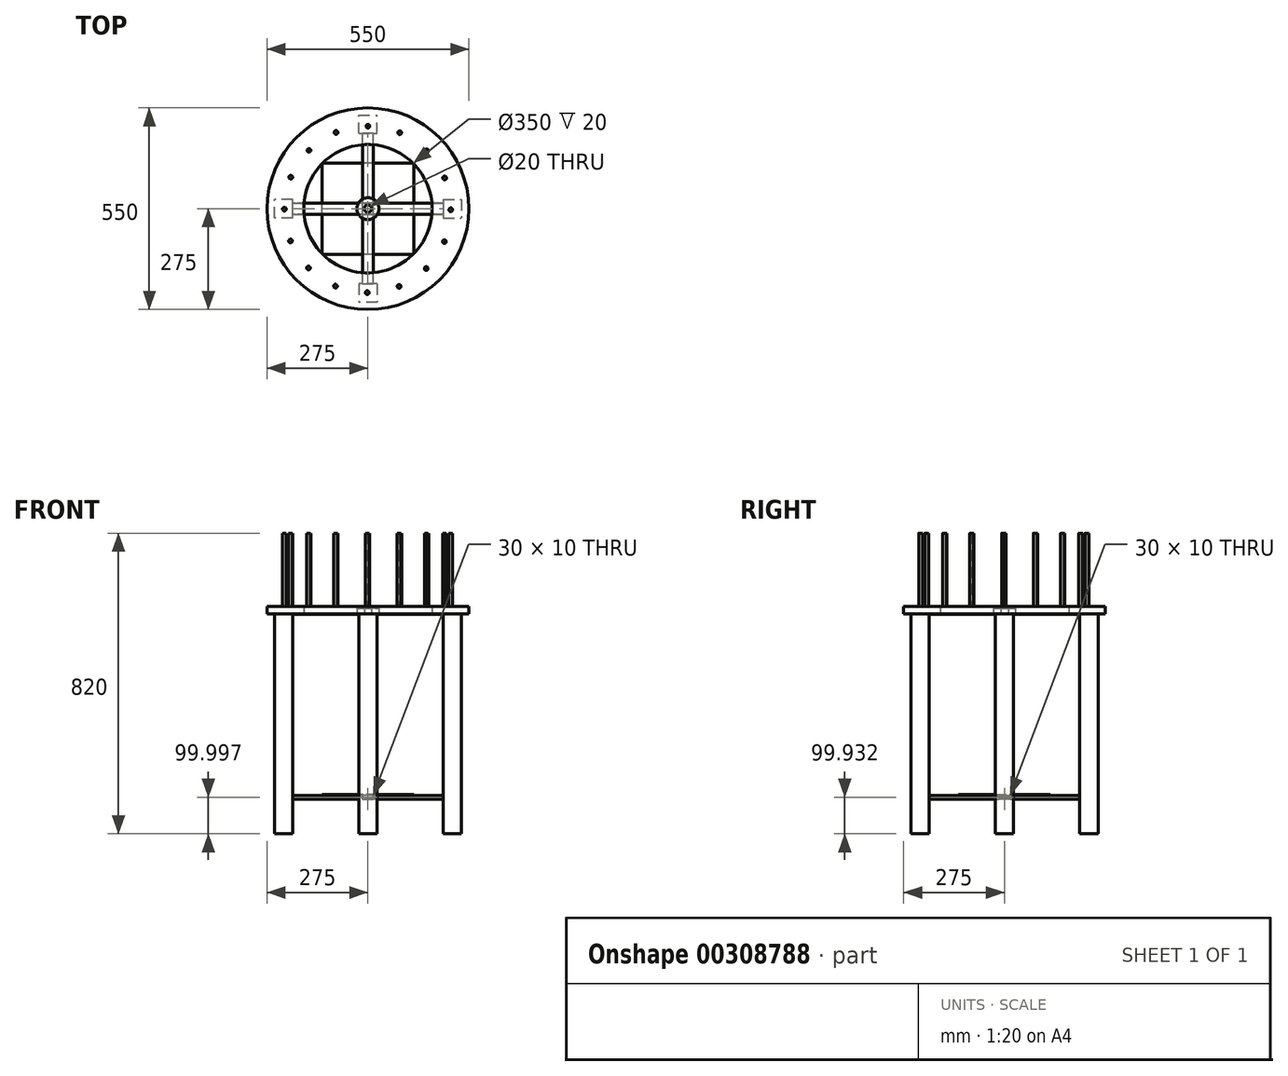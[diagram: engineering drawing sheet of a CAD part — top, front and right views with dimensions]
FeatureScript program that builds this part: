
annotation { "Feature Type Name" : "Feature", "Feature Type Description" : "" }
export const myFeature = defineFeature(function(context is Context, id is Id, definition is map)
    precondition{}
    {
        {
            var Q0;
            Q0=qCreatedBy(makeId("Top.planeOp"),FACE);
            var sketch = newSketch(context, id + "F0", { "sketchPlane" : qUnion([Q0])});
            skCircle(sketch, "E0", {"center": v(0, 0) * mm, "radius": 175 * mm});
            skCircle(sketch, "E1", {"center": v(0, 0) * mm, "radius": 5 * mm});
            skCircle(sketch, "E2", {"center": v(0, 0) * mm, "radius": 275 * mm});
            skCircle(sketch, "E3", {"center": v(0, 225) * mm, "radius": 5 * mm});
            skCircle(sketch, "E4.1.0", {"center": v(-86.9, 208.08) * mm, "radius": 5 * mm});
            skCircle(sketch, "E4.2.0", {"center": v(-160.72, 159.2) * mm, "radius": 5 * mm});
            skCircle(sketch, "E4.3.0", {"center": v(-210.2, 85.78) * mm, "radius": 5 * mm});
            skCircle(sketch, "E4.4.0", {"center": v(-227.83, -0.98) * mm, "radius": 5 * mm});
            skCircle(sketch, "E4.5.0", {"center": v(-210.91, -87.89) * mm, "radius": 5 * mm});
            skCircle(sketch, "E4.6.0", {"center": v(-162.03, -161.7) * mm, "radius": 5 * mm});
            skCircle(sketch, "E4.7.0", {"center": v(-88.61, -211.19) * mm, "radius": 5 * mm});
            skCircle(sketch, "E4.8.0", {"center": v(-1.85, -228.82) * mm, "radius": 5 * mm});
            skCircle(sketch, "E4.9.0", {"center": v(85.06, -211.9) * mm, "radius": 5 * mm});
            skCircle(sketch, "E4.10.0", {"center": v(158.87, -163) * mm, "radius": 5 * mm});
            skCircle(sketch, "E4.11.0", {"center": v(208.36, -89.6) * mm, "radius": 5 * mm});
            skCircle(sketch, "E4.12.0", {"center": v(225.98, -2.83) * mm, "radius": 5 * mm});
            skCircle(sketch, "E4.13.0", {"center": v(209.06, 84.07) * mm, "radius": 5 * mm});
            skCircle(sketch, "E4.14.0", {"center": v(160.18, 157.89) * mm, "radius": 5 * mm});
            skCircle(sketch, "E4.15.0", {"center": v(86.76, 207.37) * mm, "radius": 5 * mm});
            skPoint(sketch, "E4.center", {"position": v(-0.92, -1.9) * mm});
            skSolve(sketch);
        }
        {
            var Q0;
            Q0=makeQuery(id+"F0.imprint","IMPRINT",FACE,{"disambiguationData":[TD([[makeQuery(id+"F0.imprint","IMPRINT",EDGE,{"derivedFrom":sQuery(id+"F0.wireOp",EDGE,"E4.9.0")}),1.0]])]});
            var Q1;
            Q1=makeQuery(id+"F0.imprint","IMPRINT",FACE,{"disambiguationData":[TD([[makeQuery(id+"F0.imprint","IMPRINT",EDGE,{"derivedFrom":sQuery(id+"F0.wireOp",EDGE,"E4.8.0")}),1.0]])]});
            var Q2;
            Q2=makeQuery(id+"F0.imprint","IMPRINT",FACE,{"disambiguationData":[TD([[makeQuery(id+"F0.imprint","IMPRINT",EDGE,{"derivedFrom":sQuery(id+"F0.wireOp",EDGE,"E4.7.0")}),1.0]])]});
            var Q3;
            Q3=makeQuery(id+"F0.imprint","IMPRINT",FACE,{"disambiguationData":[TD([[makeQuery(id+"F0.imprint","IMPRINT",EDGE,{"derivedFrom":sQuery(id+"F0.wireOp",EDGE,"E4.6.0")}),1.0]])]});
            var Q4;
            Q4=makeQuery(id+"F0.imprint","IMPRINT",FACE,{"disambiguationData":[TD([[makeQuery(id+"F0.imprint","IMPRINT",EDGE,{"derivedFrom":sQuery(id+"F0.wireOp",EDGE,"E4.5.0")}),1.0]])]});
            var Q5;
            Q5=makeQuery(id+"F0.imprint","IMPRINT",FACE,{"disambiguationData":[TD([[makeQuery(id+"F0.imprint","IMPRINT",EDGE,{"derivedFrom":sQuery(id+"F0.wireOp",EDGE,"E4.4.0")}),1.0]])]});
            var Q6;
            Q6=makeQuery(id+"F0.imprint","IMPRINT",FACE,{"disambiguationData":[TD([[makeQuery(id+"F0.imprint","IMPRINT",EDGE,{"derivedFrom":sQuery(id+"F0.wireOp",EDGE,"E4.3.0")}),1.0]])]});
            var Q7;
            Q7=makeQuery(id+"F0.imprint","IMPRINT",FACE,{"disambiguationData":[TD([[makeQuery(id+"F0.imprint","IMPRINT",EDGE,{"derivedFrom":sQuery(id+"F0.wireOp",EDGE,"E4.2.0")}),1.0]])]});
            var Q8;
            Q8=makeQuery(id+"F0.imprint","IMPRINT",FACE,{"disambiguationData":[TD([[makeQuery(id+"F0.imprint","IMPRINT",EDGE,{"derivedFrom":sQuery(id+"F0.wireOp",EDGE,"E4.1.0")}),1.0]])]});
            var Q9;
            Q9=makeQuery(id+"F0.imprint","IMPRINT",FACE,{"disambiguationData":[TD([[makeQuery(id+"F0.imprint","IMPRINT",EDGE,{"derivedFrom":sQuery(id+"F0.wireOp",EDGE,"E3")}),1.0]])]});
            var Q10;
            Q10=makeQuery(id+"F0.imprint","IMPRINT",FACE,{"disambiguationData":[TD([[makeQuery(id+"F0.imprint","IMPRINT",EDGE,{"derivedFrom":sQuery(id+"F0.wireOp",EDGE,"E4.15.0")}),1.0]])]});
            var Q11;
            Q11=makeQuery(id+"F0.imprint","IMPRINT",FACE,{"disambiguationData":[TD([[makeQuery(id+"F0.imprint","IMPRINT",EDGE,{"derivedFrom":sQuery(id+"F0.wireOp",EDGE,"E4.14.0")}),1.0]])]});
            var Q12;
            Q12=makeQuery(id+"F0.imprint","IMPRINT",FACE,{"disambiguationData":[TD([[makeQuery(id+"F0.imprint","IMPRINT",EDGE,{"derivedFrom":sQuery(id+"F0.wireOp",EDGE,"E4.13.0")}),1.0]])]});
            var Q13;
            Q13=makeQuery(id+"F0.imprint","IMPRINT",FACE,{"disambiguationData":[TD([[makeQuery(id+"F0.imprint","IMPRINT",EDGE,{"derivedFrom":sQuery(id+"F0.wireOp",EDGE,"E4.12.0")}),1.0]])]});
            var Q14;
            Q14=makeQuery(id+"F0.imprint","IMPRINT",FACE,{"disambiguationData":[TD([[makeQuery(id+"F0.imprint","IMPRINT",EDGE,{"derivedFrom":sQuery(id+"F0.wireOp",EDGE,"E4.11.0")}),1.0]])]});
            var Q15;
            Q15=makeQuery(id+"F0.imprint","IMPRINT",FACE,{"disambiguationData":[TD([[makeQuery(id+"F0.imprint","IMPRINT",EDGE,{"derivedFrom":sQuery(id+"F0.wireOp",EDGE,"E4.10.0")}),1.0]])]});
            var Q16;
            Q16=makeQuery(id+"F0.imprint","IMPRINT",FACE,{"disambiguationData":[TD([[makeQuery(id+"F0.imprint","IMPRINT",EDGE,{"derivedFrom":sQuery(id+"F0.wireOp",EDGE,"E0")}),-1.0]])]});
            extrude(context, id + "F1", {"entities" : qUnion([Q0, Q1, Q2, Q3, Q4, Q5, Q6, Q7, Q8, Q9, Q10, Q11, Q12, Q13, Q14, Q15, Q16]), "depth" : 20 * mm});
        }
        {
            var Q0;
            Q0=makeQuery(id+"F0.imprint","IMPRINT",FACE,{"disambiguationData":[TD([[makeQuery(id+"F0.imprint","IMPRINT",EDGE,{"derivedFrom":sQuery(id+"F0.wireOp",EDGE,"E4.2.0")}),1.0]])]});
            var Q1;
            Q1=makeQuery(id+"F0.imprint","IMPRINT",FACE,{"disambiguationData":[TD([[makeQuery(id+"F0.imprint","IMPRINT",EDGE,{"derivedFrom":sQuery(id+"F0.wireOp",EDGE,"E4.3.0")}),1.0]])]});
            var Q2;
            Q2=makeQuery(id+"F0.imprint","IMPRINT",FACE,{"disambiguationData":[TD([[makeQuery(id+"F0.imprint","IMPRINT",EDGE,{"derivedFrom":sQuery(id+"F0.wireOp",EDGE,"E4.1.0")}),1.0]])]});
            var Q3;
            Q3=makeQuery(id+"F0.imprint","IMPRINT",FACE,{"disambiguationData":[TD([[makeQuery(id+"F0.imprint","IMPRINT",EDGE,{"derivedFrom":sQuery(id+"F0.wireOp",EDGE,"E3")}),1.0]])]});
            var Q4;
            Q4=makeQuery(id+"F0.imprint","IMPRINT",FACE,{"disambiguationData":[TD([[makeQuery(id+"F0.imprint","IMPRINT",EDGE,{"derivedFrom":sQuery(id+"F0.wireOp",EDGE,"E4.15.0")}),1.0]])]});
            var Q5;
            Q5=makeQuery(id+"F0.imprint","IMPRINT",FACE,{"disambiguationData":[TD([[makeQuery(id+"F0.imprint","IMPRINT",EDGE,{"derivedFrom":sQuery(id+"F0.wireOp",EDGE,"E4.14.0")}),1.0]])]});
            var Q6;
            Q6=makeQuery(id+"F0.imprint","IMPRINT",FACE,{"disambiguationData":[TD([[makeQuery(id+"F0.imprint","IMPRINT",EDGE,{"derivedFrom":sQuery(id+"F0.wireOp",EDGE,"E4.13.0")}),1.0]])]});
            var Q7;
            Q7=makeQuery(id+"F0.imprint","IMPRINT",FACE,{"disambiguationData":[TD([[makeQuery(id+"F0.imprint","IMPRINT",EDGE,{"derivedFrom":sQuery(id+"F0.wireOp",EDGE,"E4.12.0")}),1.0]])]});
            var Q8;
            Q8=makeQuery(id+"F0.imprint","IMPRINT",FACE,{"disambiguationData":[TD([[makeQuery(id+"F0.imprint","IMPRINT",EDGE,{"derivedFrom":sQuery(id+"F0.wireOp",EDGE,"E4.11.0")}),1.0]])]});
            var Q9;
            Q9=makeQuery(id+"F0.imprint","IMPRINT",FACE,{"disambiguationData":[TD([[makeQuery(id+"F0.imprint","IMPRINT",EDGE,{"derivedFrom":sQuery(id+"F0.wireOp",EDGE,"E4.10.0")}),1.0]])]});
            var Q10;
            Q10=makeQuery(id+"F0.imprint","IMPRINT",FACE,{"disambiguationData":[TD([[makeQuery(id+"F0.imprint","IMPRINT",EDGE,{"derivedFrom":sQuery(id+"F0.wireOp",EDGE,"E4.9.0")}),1.0]])]});
            var Q11;
            Q11=makeQuery(id+"F0.imprint","IMPRINT",FACE,{"disambiguationData":[TD([[makeQuery(id+"F0.imprint","IMPRINT",EDGE,{"derivedFrom":sQuery(id+"F0.wireOp",EDGE,"E4.7.0")}),1.0]])]});
            var Q12;
            Q12=makeQuery(id+"F0.imprint","IMPRINT",FACE,{"disambiguationData":[TD([[makeQuery(id+"F0.imprint","IMPRINT",EDGE,{"derivedFrom":sQuery(id+"F0.wireOp",EDGE,"E4.8.0")}),1.0]])]});
            var Q13;
            Q13=makeQuery(id+"F0.imprint","IMPRINT",FACE,{"disambiguationData":[TD([[makeQuery(id+"F0.imprint","IMPRINT",EDGE,{"derivedFrom":sQuery(id+"F0.wireOp",EDGE,"E4.6.0")}),1.0]])]});
            var Q14;
            Q14=makeQuery(id+"F0.imprint","IMPRINT",FACE,{"disambiguationData":[TD([[makeQuery(id+"F0.imprint","IMPRINT",EDGE,{"derivedFrom":sQuery(id+"F0.wireOp",EDGE,"E4.5.0")}),1.0]])]});
            var Q15;
            Q15=makeQuery(id+"F0.imprint","IMPRINT",FACE,{"disambiguationData":[TD([[makeQuery(id+"F0.imprint","IMPRINT",EDGE,{"derivedFrom":sQuery(id+"F0.wireOp",EDGE,"E4.4.0")}),1.0]])]});
            extrude(context, id + "F2", {"entities" : qUnion([Q0, Q1, Q2, Q3, Q4, Q5, Q6, Q7, Q8, Q9, Q10, Q11, Q12, Q13, Q14, Q15]), "operationType" : NewBodyOperationType.ADD, "depth" : 220 * mm});
        }
        {
            var Q0;
            Q0=qCreatedBy(makeId("Top.planeOp"),FACE);
            var sketch = newSketch(context, id + "F3", { "sketchPlane" : qUnion([Q0])});
            skLineSegment(sketch, "E5.bottom", {"start": v(25, -205.13) * mm, "end": v(-25, -205.13) * mm});
            skLineSegment(sketch, "E5.top", {"start": v(25, -255.13) * mm, "end": v(-25, -255.13) * mm});
            skLineSegment(sketch, "E5.left", {"start": v(25, -205.13) * mm, "end": v(25, -255.13) * mm});
            skLineSegment(sketch, "E5.right", {"start": v(-25, -205.13) * mm, "end": v(-25, -255.13) * mm});
            skPoint(sketch, "E5.middle", {"position": v(0, -230.13) * mm});
            skLineSegment(sketch, "E6.1.0", {"start": v(255.13, 25) * mm, "end": v(255.13, -25) * mm});
            skLineSegment(sketch, "E6.1.1", {"start": v(205.13, 25) * mm, "end": v(205.13, -25) * mm});
            skLineSegment(sketch, "E6.1.2", {"start": v(205.13, -25) * mm, "end": v(255.13, -25) * mm});
            skLineSegment(sketch, "E6.1.3", {"start": v(205.13, 25) * mm, "end": v(255.13, 25) * mm});
            skLineSegment(sketch, "E6.2.0", {"start": v(-25, 255.13) * mm, "end": v(25, 255.13) * mm});
            skLineSegment(sketch, "E6.2.1", {"start": v(-25, 205.13) * mm, "end": v(25, 205.13) * mm});
            skLineSegment(sketch, "E6.2.2", {"start": v(25, 205.13) * mm, "end": v(25, 255.13) * mm});
            skLineSegment(sketch, "E6.2.3", {"start": v(-25, 205.13) * mm, "end": v(-25, 255.13) * mm});
            skLineSegment(sketch, "E6.3.0", {"start": v(-255.13, -25) * mm, "end": v(-255.13, 25) * mm});
            skLineSegment(sketch, "E6.3.1", {"start": v(-205.13, -25) * mm, "end": v(-205.13, 25) * mm});
            skLineSegment(sketch, "E6.3.2", {"start": v(-205.13, 25) * mm, "end": v(-255.13, 25) * mm});
            skLineSegment(sketch, "E6.3.3", {"start": v(-205.13, -25) * mm, "end": v(-255.13, -25) * mm});
            skPoint(sketch, "E6.center", {"position": v(0, 0) * mm});
            skSolve(sketch);
        }
        {
            var Q0;
            Q0 = qSketchRegion(id + "F3", true);
            extrude(context, id + "F4", {"entities" : qUnion([Q0]), "operationType" : NewBodyOperationType.ADD, "oppositeDirection" : true, "depth" : 600 * mm});
        }
        {
            var Q0;
            Q0=qCreatedBy(makeId("Right.planeOp"),FACE);
            var sketch = newSketch(context, id + "F5", { "sketchPlane" : qUnion([Q0])});
            skLineSegment(sketch, "E7.bottom", {"start": v(15, -505.07) * mm, "end": v(-15, -505.07) * mm});
            skLineSegment(sketch, "E7.top", {"start": v(15, -495.07) * mm, "end": v(-15, -495.07) * mm});
            skLineSegment(sketch, "E7.left", {"start": v(15, -505.07) * mm, "end": v(15, -495.07) * mm});
            skLineSegment(sketch, "E7.right", {"start": v(-15, -505.07) * mm, "end": v(-15, -495.07) * mm});
            skPoint(sketch, "E7.middle", {"position": v(0, -500.07) * mm});
            skPoint(sketch, "E8.orphan", {"position": v(0, -600.07) * mm});
            skSolve(sketch);
        }
        {
            var Q0;
            Q0 = qSketchRegion(id + "F5", true);
            extrude(context, id + "F6", {"entities" : qUnion([Q0]), "operationType" : NewBodyOperationType.ADD, "endBound" : BoundingType.SYMMETRIC, "depth" : 440 * mm});
        }
        {
            var Q0;
            Q0=qCreatedBy(makeId("Front.planeOp"),FACE);
            var sketch = newSketch(context, id + "F7", { "sketchPlane" : qUnion([Q0])});
            skLineSegment(sketch, "E9.bottom", {"start": v(15, -505) * mm, "end": v(-15, -505) * mm});
            skLineSegment(sketch, "E9.top", {"start": v(15, -495) * mm, "end": v(-15, -495) * mm});
            skLineSegment(sketch, "E9.left", {"start": v(15, -505) * mm, "end": v(15, -495) * mm});
            skLineSegment(sketch, "E9.right", {"start": v(-15, -505) * mm, "end": v(-15, -495) * mm});
            skPoint(sketch, "E9.middle", {"position": v(0, -500) * mm});
            skPoint(sketch, "E10.orphan", {"position": v(0, -600) * mm});
            skSolve(sketch);
        }
        {
            var Q0;
            Q0 = qSketchRegion(id + "F7", true);
            extrude(context, id + "F8", {"entities" : qUnion([Q0]), "operationType" : NewBodyOperationType.ADD, "endBound" : BoundingType.SYMMETRIC, "depth" : 440 * mm});
        }
        {
            var Q0;
            Q0=qCreatedBy(makeId("Front.planeOp"),FACE);
            var sketch = newSketch(context, id + "F9", { "sketchPlane" : qUnion([Q0])});
            skLineSegment(sketch, "E11.bottom", {"start": v(125, -495.14) * mm, "end": v(-125, -495.14) * mm});
            skLineSegment(sketch, "E11.top", {"start": v(125, -492.34) * mm, "end": v(-125, -492.34) * mm});
            skLineSegment(sketch, "E11.left", {"start": v(125, -495.14) * mm, "end": v(125, -492.34) * mm});
            skLineSegment(sketch, "E11.right", {"start": v(-125, -495.14) * mm, "end": v(-125, -492.34) * mm});
            skPoint(sketch, "E11.middle", {"position": v(0, -493.74) * mm});
            skPoint(sketch, "E12.orphan", {"position": v(0, -600.04) * mm});
            skSolve(sketch);
        }
        {
            var Q0;
            Q0 = qSketchRegion(id + "F9", true);
            extrude(context, id + "F10", {"entities" : qUnion([Q0]), "endBound" : BoundingType.SYMMETRIC, "depth" : 250 * mm});
        }
        {
            var Q0;
            Q0=qCreatedBy(makeId("Front.planeOp"),FACE);
            var sketch = newSketch(context, id + "F11", { "sketchPlane" : qUnion([Q0])});
            skLineSegment(sketch, "E13.bottom", {"start": v(220, 1.5) * mm, "end": v(-220, 1.5) * mm});
            skLineSegment(sketch, "E13.top", {"start": v(220, -1.5) * mm, "end": v(-220, -1.5) * mm});
            skLineSegment(sketch, "E13.left", {"start": v(220, 1.5) * mm, "end": v(220, -1.5) * mm});
            skLineSegment(sketch, "E13.right", {"start": v(-220, 1.5) * mm, "end": v(-220, -1.5) * mm});
            skPoint(sketch, "E13.middle", {"position": v(0, 0) * mm});
            skSolve(sketch);
        }
        {
            var Q0;
            Q0 = qSketchRegion(id + "F11", true);
            extrude(context, id + "F12", {"entities" : qUnion([Q0]), "operationType" : NewBodyOperationType.ADD, "endBound" : BoundingType.SYMMETRIC, "depth" : 30 * mm});
        }
        {
            var Q0;
            Q0=qCreatedBy(makeId("Right.planeOp"),FACE);
            var sketch = newSketch(context, id + "F13", { "sketchPlane" : qUnion([Q0])});
            skLineSegment(sketch, "E14.bottom", {"start": v(-220, -1.5) * mm, "end": v(220, -1.5) * mm});
            skLineSegment(sketch, "E14.top", {"start": v(-220, 1.5) * mm, "end": v(220, 1.5) * mm});
            skLineSegment(sketch, "E14.left", {"start": v(-220, -1.5) * mm, "end": v(-220, 1.5) * mm});
            skLineSegment(sketch, "E14.right", {"start": v(220, -1.5) * mm, "end": v(220, 1.5) * mm});
            skPoint(sketch, "E14.middle", {"position": v(0, 0) * mm});
            skSolve(sketch);
        }
        {
            var Q0;
            Q0 = qSketchRegion(id + "F13", true);
            extrude(context, id + "F14", {"entities" : qUnion([Q0]), "operationType" : NewBodyOperationType.ADD, "endBound" : BoundingType.SYMMETRIC, "depth" : 30 * mm});
        }
        {
            var Q0;
            Q0=qCreatedBy(makeId("Top.planeOp"),FACE);
            var sketch = newSketch(context, id + "F15", { "sketchPlane" : qUnion([Q0])});
            skCircle(sketch, "E15", {"center": v(0, 0) * mm, "radius": 30 * mm});
            skCircle(sketch, "E16", {"center": v(0, 0) * mm, "radius": 10 * mm});
            skSolve(sketch);
        }
        {
            var Q0;
            Q0=makeQuery(id+"F15.imprint","IMPRINT",FACE,{"disambiguationData":[TD([[makeQuery(id+"F15.imprint","IMPRINT",EDGE,{"derivedFrom":sQuery(id+"F15.wireOp",EDGE,"E15")}),1.0]])]});
            extrude(context, id + "F16", {"entities" : qUnion([Q0]), "operationType" : NewBodyOperationType.ADD, "depth" : 15 * mm});
        }
        {
            var Q0;
            Q0=makeQuery(id+"F16.boolean.opBoolean","SPLIT",FACE,{"disambiguationData":[TD([makeQuery(id+"F16.opExtrude","SWEPT_FACE",FACE,{"disambiguationData":[OSD([sQuery(id+"F15.wireOp",EDGE,"E16")])]})])],"derivedFrom":makeQuery(id+"F14.boolean.opBoolean","MERGE",FACE,{"derivedFrom":[makeQuery(id+"F12.opExtrude","SWEPT_FACE",FACE,{"disambiguationData":[OSD([sQuery(id+"F11.wireOp",EDGE,"E13.bottom")])]}),makeQuery(id+"F14.opExtrude","SWEPT_FACE",FACE,{"disambiguationData":[OSD([sQuery(id+"F13.wireOp",EDGE,"E14.top")])]})]})});
            extrude(context, id + "F17", {"entities" : qUnion([Q0]), "operationType" : NewBodyOperationType.REMOVE, "endBound" : BoundingType.SYMMETRIC, "oppositeDirection" : true, "depth" : 250 * mm});
        }
    });
